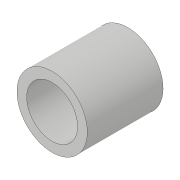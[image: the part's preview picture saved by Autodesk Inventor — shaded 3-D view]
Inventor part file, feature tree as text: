
AUTODESK INVENTOR PART (.ipt)
format: ipt  version: 2018.3 (Build 223284000, 284)  size: 83,968 bytes
history: native  units: in
note: dims shown in document units (in); Inventor stores cm internally (conversion verified against a paired STEP export)
features: extrude x1, sketch x1
ambient origin geometry x8: Origin, YZ Plane, XZ Plane, XY Plane, X Axis, Y Axis, Z Axis, Center Point
bodies: Solid1 (feature_tree)
feature tree (2):
  extrude  "Extrusion1"  Depth=0.743in
  sketch  "Sketch1"  dims[d0=0.5in d1=0.69in d2=0.743in d3=0.0in]
